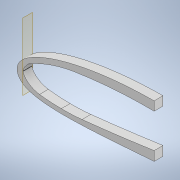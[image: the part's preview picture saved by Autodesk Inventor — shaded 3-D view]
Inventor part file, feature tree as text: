
AUTODESK INVENTOR PART (.ipt)
format: ipt  version: 2022.3 (Build 263350000, 350)  size: 512,000 bytes
history: native  units: mm
features: sketch x6, extrude x5, thicken_offset x3, fillet x2, projected_geometry x2, shell x1, plane x1, other x1
ambient origin geometry x8: Origin, YZ Plane, XZ Plane, XY Plane, X Axis, Y Axis, Z Axis, Center Point
bodies: Solid1 (feature_tree)
feature tree (21):
  extrude  "Extrusion1"  Depth=10.0mm
  shell  "Shell1"  Thickness=1.0mm
  thicken_offset  "Thicken1"
  extrude  "Extrusion27"  TaperAngle=0.0deg  [1 undecoded]
  thicken_offset  "Thicken3"
  extrude  "Extrusion29"  Depth=20.0mm
  plane  "Work Plane5"
  other  "Bend Part2"
  thicken_offset  "Thicken5"
  extrude  "Extrusion30"  Depth=10.0mm TaperAngle=0.0deg
  extrude  "Extrusion31"  Depth=150.0mm
  fillet  "Fillet6"  Radius=1.0mm
  fillet  "Fillet8"  Radius=150.0mm
  sketch  "Sketch3"  dims[d0=10.0mm d1=0.0mm d2=3.0mm d159=1.0mm d160=2.0mm]
  sketch  "Sketch48"  dims[d236=190.0mm d237=0.0mm d238=0.0mm]
  sketch  "Sketch55"  dims[d249=2.0mm d250=1.0mm d254=20.0mm]
  projected_geometry  "Projected Loop32"
  sketch  "Sketch57"  dims[d255=8.0mm d256=10.0mm d257=0.0mm]
  sketch  "Sketch58"  dims[d262=10.0mm d263=0.523599mm d264=1.0mm d265=1.0mm d268=150.0mm]
  projected_geometry  "Projected Loop34"
  sketch  "Sketch59"  dims[d269=6.0mm d270=10.0mm d271=0.0mm d272=150.0mm d273=100.0mm d274=0.0mm d275=550.0mm d276=130.0mm d277=9.0mm d278=2000.0mm d279=200.0mm d281=150.0mm]
note: 1 required parameter value undecoded (feature->parameter linkage not recoverable at this tier; creation-order binding heuristic only, values carry confidence <= 0.55)
